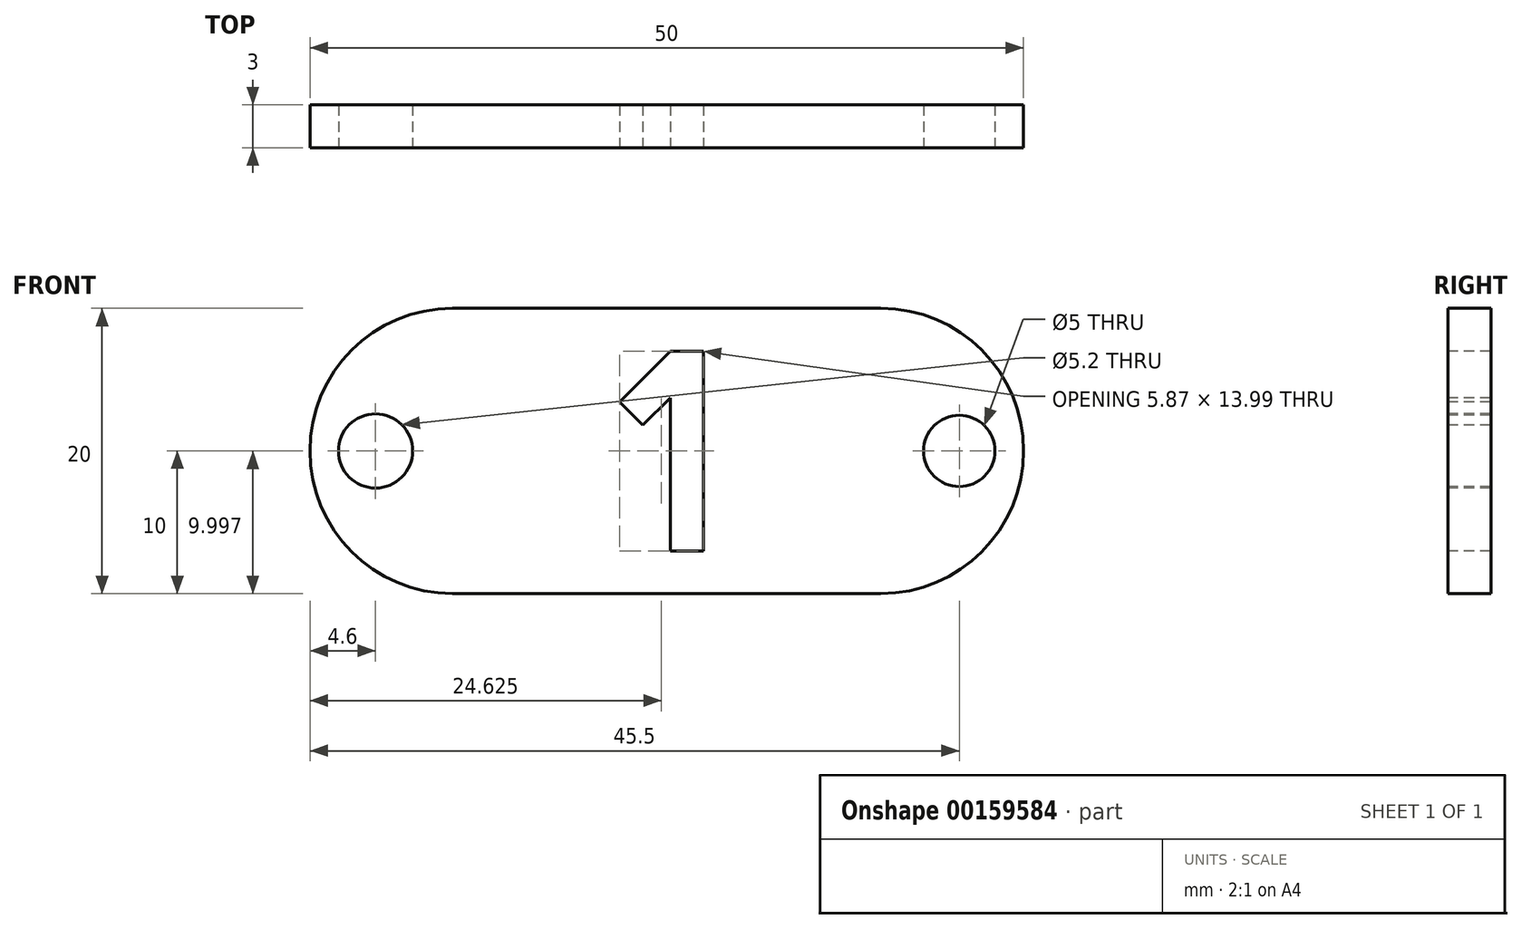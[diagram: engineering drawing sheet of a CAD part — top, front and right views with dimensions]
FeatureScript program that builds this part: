
annotation { "Feature Type Name" : "Feature", "Feature Type Description" : "" }
export const myFeature = defineFeature(function(context is Context, id is Id, definition is map)
    precondition{}
    {
        {
            var Q0;
            Q0=qCreatedBy(makeId("Front.planeOp"),FACE);
            var sketch = newSketch(context, id + "F0", { "sketchPlane" : qUnion([Q0])});
            skLineSegment(sketch, "E0.bottom", {"start": v(25, 10) * mm, "end": v(-25, 10) * mm});
            skLineSegment(sketch, "E0.top", {"start": v(25, -10) * mm, "end": v(-25, -10) * mm});
            skLineSegment(sketch, "E0.left", {"start": v(25, 10) * mm, "end": v(25, -10) * mm});
            skLineSegment(sketch, "E0.right", {"start": v(-25, 10) * mm, "end": v(-25, -10) * mm});
            skPoint(sketch, "E0.middle", {"position": v(0, 0) * mm});
            skSolve(sketch);
        }
        {
            var Q0;
            Q0=makeQuery(id+"F0.imprint","IMPRINT",FACE,{"disambiguationData":[TD([[makeQuery(id+"F0.imprint","IMPRINT",EDGE,{"derivedFrom":sQuery(id+"F0.wireOp",EDGE,"E0.bottom")}),1.0]])]});
            extrude(context, id + "F1", {"entities" : qUnion([Q0]), "depth" : 3 * mm});
        }
        {
            var Q0;
            Q0=makeQuery(id+"F1.opExtrude","CAP_FACE",FACE,{"disambiguationData":[OSD([sQuery(id+"F0.wireOp",EDGE,"E0.bottom"),sQuery(id+"F0.wireOp",EDGE,"E0.top"),sQuery(id+"F0.wireOp",EDGE,"E0.left"),sQuery(id+"F0.wireOp",EDGE,"E0.right")])],"isStart":false});
            var sketch = newSketch(context, id + "F2", { "sketchPlane" : qUnion([Q0])});
            skText(sketch, "E1", { "text": "1", "fontName": "AllertaStencil-Regular.ttf"});
            skLineSegment(sketch, "E2", {"start": v(-3.86, 0) * mm, "end": v(3.86, 0) * mm, "construction": true});
            skPoint(sketch, "E3", {"position": v(0, 0) * mm});
            skCircle(sketch, "E4", {"center": v(20.5, 0) * mm, "radius": 2.5 * mm});
            skCircle(sketch, "E5", {"center": v(-20.4, 0) * mm, "radius": 2.6 * mm});
            const initialGuessF2  = {"E1": [-0.00386, -0.007, 1, 0, 0.014]};
            skSetInitialGuess(sketch, initialGuessF2);
            skSolve(sketch);
        }
        {
            var Q0;
            Q0=qSketchRegion(id+"F2",true);
            extrude(context, id + "F3", {"entities" : qUnion([Q0]), "operationType" : NewBodyOperationType.REMOVE, "endBound" : BoundingType.THROUGH_ALL, "oppositeDirection" : true, "depth" : 25 * mm});
        }
        {
            var Q0;
            Q0=makeQuery(id+"F1.opExtrude","SWEPT_EDGE",EDGE,{"disambiguationData":[OSD([sQuery(id+"F0.wireOp",EDGE,"E0.bottom"),sQuery(id+"F0.wireOp",EDGE,"E0.right")])]});
            var Q1;
            Q1=makeQuery(id+"F1.opExtrude","SWEPT_EDGE",EDGE,{"disambiguationData":[OSD([sQuery(id+"F0.wireOp",EDGE,"E0.top"),sQuery(id+"F0.wireOp",EDGE,"E0.right")])]});
            var Q2;
            Q2=makeQuery(id+"F1.opExtrude","SWEPT_EDGE",EDGE,{"disambiguationData":[OSD([sQuery(id+"F0.wireOp",EDGE,"E0.bottom"),sQuery(id+"F0.wireOp",EDGE,"E0.left")])]});
            var Q3;
            Q3=makeQuery(id+"F1.opExtrude","SWEPT_EDGE",EDGE,{"disambiguationData":[OSD([sQuery(id+"F0.wireOp",EDGE,"E0.top"),sQuery(id+"F0.wireOp",EDGE,"E0.left")])]});
            fillet(context, id + "F4", {"entities" : qUnion([Q0, Q1, Q2, Q3]), "radius" : 10 * mm, "tangentPropagation" : true, "allowEdgeOverflow" : false});
        }
    });
